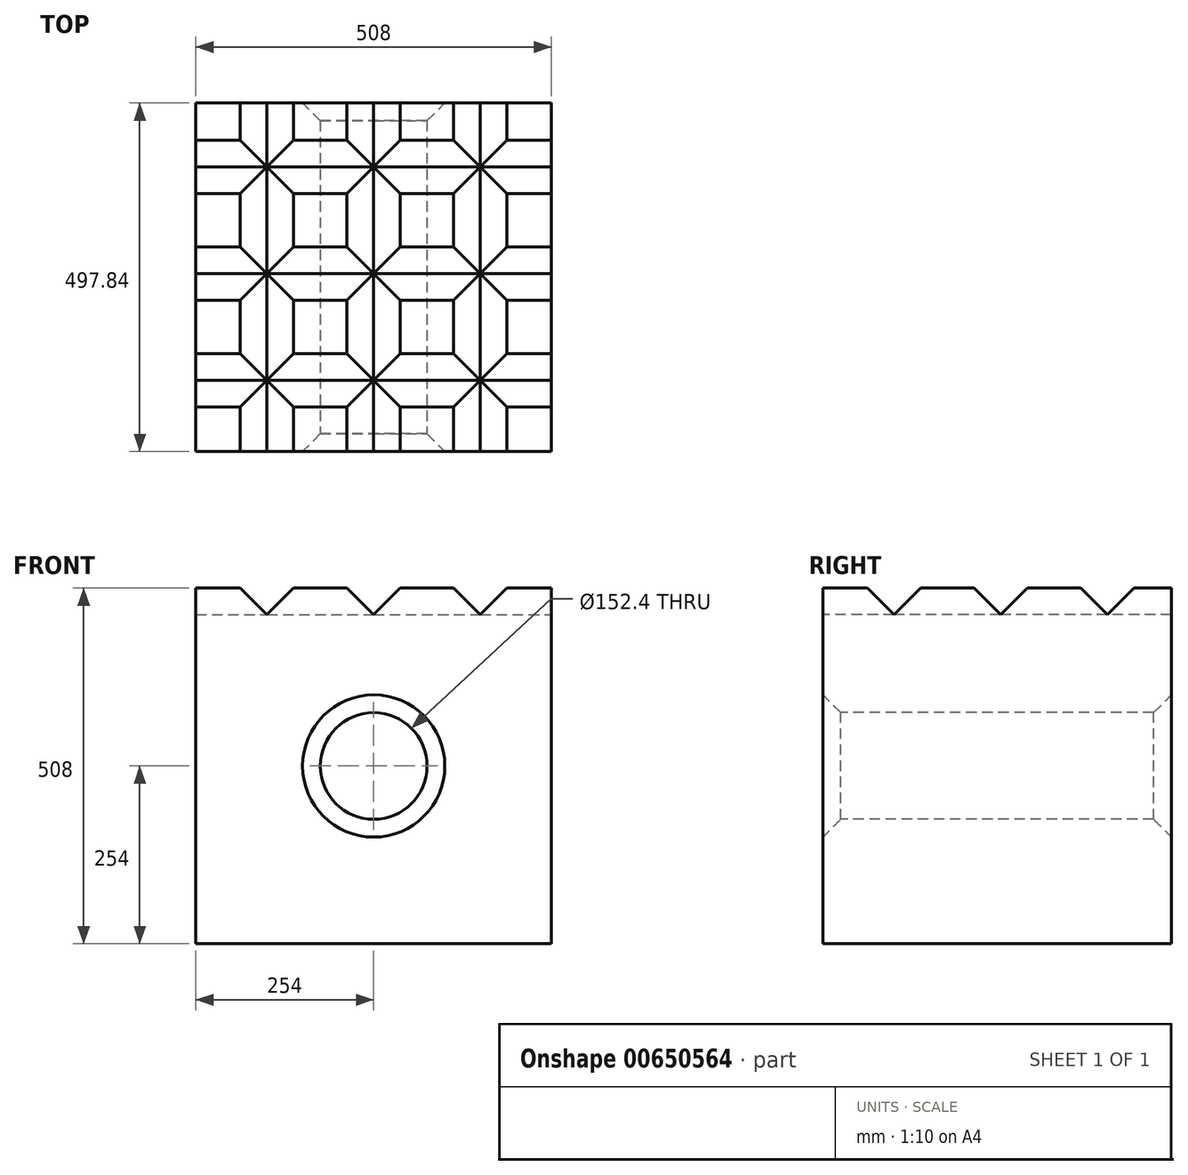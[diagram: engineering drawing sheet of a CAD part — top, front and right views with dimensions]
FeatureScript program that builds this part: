
annotation { "Feature Type Name" : "Feature", "Feature Type Description" : "" }
export const myFeature = defineFeature(function(context is Context, id is Id, definition is map)
    precondition{}
    {
        {
            var Q0;
            Q0=qCreatedBy(makeId("Front.planeOp"),FACE);
            var sketch = newSketch(context, id + "F0", { "sketchPlane" : qUnion([Q0])});
            skLineSegment(sketch, "E0.bottom", {"start": v(-254, -254) * mm, "end": v(254, -254) * mm});
            skLineSegment(sketch, "E0.top", {"start": v(-254, 254) * mm, "end": v(254, 254) * mm});
            skLineSegment(sketch, "E0.left", {"start": v(-254, -254) * mm, "end": v(-254, 254) * mm});
            skLineSegment(sketch, "E0.right", {"start": v(254, -254) * mm, "end": v(254, 254) * mm});
            skPoint(sketch, "E0.middle", {"position": v(0, 0) * mm});
            skSolve(sketch);
        }
        {
            var Q0;
            Q0=makeQuery(id+"F0.imprint","IMPRINT",FACE,{"disambiguationData":[TD([[makeQuery(id+"F0.imprint","IMPRINT",EDGE,{"derivedFrom":sQuery(id+"F0.wireOp",EDGE,"E0.bottom")}),1.0]])]});
            extrude(context, id + "F1", {"entities" : qUnion([Q0]), "depth" : 497.84 * mm, "offsetDistance" : 25.4 * mm});
        }
        {
            var Q0;
            Q0=makeQuery(id+"F1.opExtrude","CAP_FACE",FACE,{"disambiguationData":[OSD([sQuery(id+"F0.wireOp",EDGE,"E0.bottom"),sQuery(id+"F0.wireOp",EDGE,"E0.top"),sQuery(id+"F0.wireOp",EDGE,"E0.left"),sQuery(id+"F0.wireOp",EDGE,"E0.right")])],"isStart":false});
            var sketch = newSketch(context, id + "F2", { "sketchPlane" : qUnion([Q0])});
            skCircle(sketch, "E1", {"center": v(0, 0) * mm, "radius": 76.2 * mm});
            skSolve(sketch);
        }
        {
            var Q0;
            Q0=makeQuery(id+"F2.imprint","IMPRINT",FACE,{"disambiguationData":[TD([[makeQuery(id+"F2.imprint","IMPRINT",EDGE,{"derivedFrom":sQuery(id+"F2.wireOp",EDGE,"E1")}),1.0]])]});
            extrude(context, id + "F3", {"entities" : qUnion([Q0]), "operationType" : NewBodyOperationType.REMOVE, "endBound" : BoundingType.SYMMETRIC, "oppositeDirection" : true, "depth" : 1356.5 * mm, "offsetDistance" : 25.4 * mm});
        }
        {
            var Q0;
            Q0=makeQuery(id+"F3.boolean.opBoolean","INTERSECT",EDGE,{"derivedFrom":[makeQuery(id+"F1.opExtrude","CAP_FACE",FACE,{"disambiguationData":[OSD([sQuery(id+"F0.wireOp",EDGE,"E0.bottom"),sQuery(id+"F0.wireOp",EDGE,"E0.top"),sQuery(id+"F0.wireOp",EDGE,"E0.left"),sQuery(id+"F0.wireOp",EDGE,"E0.right")])],"isStart":false}),makeQuery(id+"F3.opExtrude","SWEPT_FACE",FACE,{"disambiguationData":[OSD([sQuery(id+"F2.wireOp",EDGE,"E1")])]})]});
            var Q1;
            Q1=makeQuery(id+"F3.boolean.opBoolean","INTERSECT",EDGE,{"derivedFrom":[makeQuery(id+"F1.opExtrude","CAP_FACE",FACE,{"disambiguationData":[OSD([sQuery(id+"F0.wireOp",EDGE,"E0.bottom"),sQuery(id+"F0.wireOp",EDGE,"E0.top"),sQuery(id+"F0.wireOp",EDGE,"E0.left"),sQuery(id+"F0.wireOp",EDGE,"E0.right")])],"isStart":true}),makeQuery(id+"F3.opExtrude","SWEPT_FACE",FACE,{"disambiguationData":[OSD([sQuery(id+"F2.wireOp",EDGE,"E1")])]})]});
            chamfer(context, id + "F4", {"entities" : qUnion([Q0, Q1]), "width" : 25.4 * mm, "tangentPropagation" : true});
        }
        {
            var Q0;
            Q0=qCreatedBy(makeId("Front.planeOp"),FACE);
            var sketch = newSketch(context, id + "F5", { "sketchPlane" : qUnion([Q0])});
            skLineSegment(sketch, "E2", {"start": v(-152.4, 215.9) * mm, "end": v(-98.52, 269.78) * mm});
            skLineSegment(sketch, "E3", {"start": v(-98.52, 269.78) * mm, "end": v(-206.28, 269.78) * mm});
            skLineSegment(sketch, "E4", {"start": v(-206.28, 269.78) * mm, "end": v(-152.4, 215.9) * mm});
            skSolve(sketch);
        }
        {
            var Q0;
            Q0=makeQuery(id+"F5.imprint","IMPRINT",FACE,{"disambiguationData":[TD([[makeQuery(id+"F5.imprint","IMPRINT",EDGE,{"derivedFrom":sQuery(id+"F5.wireOp",EDGE,"E2")}),1.0]])]});
            extrude(context, id + "F6", {"entities" : qUnion([Q0]), "operationType" : NewBodyOperationType.REMOVE, "endBound" : BoundingType.SYMMETRIC, "oppositeDirection" : true, "depth" : 1270 * mm, "offsetDistance" : 25.4 * mm});
        }
        {
            var Q0;
            Q0=qCreatedBy(makeId("Front.planeOp"),FACE);
            var sketch = newSketch(context, id + "F7", { "sketchPlane" : qUnion([Q0])});
            skLineSegment(sketch, "E5", {"start": v(0, 215.9) * mm, "end": v(53.88, 269.78) * mm});
            skLineSegment(sketch, "E6", {"start": v(53.88, 269.78) * mm, "end": v(-53.88, 269.78) * mm});
            skLineSegment(sketch, "E7", {"start": v(-53.88, 269.78) * mm, "end": v(0, 215.9) * mm});
            skSolve(sketch);
        }
        {
            var Q0;
            Q0 = qSketchRegion(id + "F7", true);
            extrude(context, id + "F8", {"entities" : qUnion([Q0]), "operationType" : NewBodyOperationType.REMOVE, "endBound" : BoundingType.SYMMETRIC, "oppositeDirection" : true, "depth" : 1270 * mm, "offsetDistance" : 25.4 * mm});
        }
        {
            var Q0;
            Q0=qCreatedBy(makeId("Front.planeOp"),FACE);
            var sketch = newSketch(context, id + "F9", { "sketchPlane" : qUnion([Q0])});
            skLineSegment(sketch, "E8", {"start": v(152.4, 215.9) * mm, "end": v(206.28, 269.78) * mm});
            skLineSegment(sketch, "E9", {"start": v(206.28, 269.78) * mm, "end": v(98.52, 269.78) * mm});
            skLineSegment(sketch, "E10", {"start": v(152.4, 215.9) * mm, "end": v(98.52, 269.78) * mm});
            skSolve(sketch);
        }
        {
            var Q0;
            Q0 = qSketchRegion(id + "F9", true);
            extrude(context, id + "F10", {"entities" : qUnion([Q0]), "operationType" : NewBodyOperationType.REMOVE, "endBound" : BoundingType.SYMMETRIC, "oppositeDirection" : true, "depth" : 1270 * mm, "offsetDistance" : 25.4 * mm});
        }
        {
            var Q0;
            Q0=qCreatedBy(makeId("Right.planeOp"),FACE);
            var sketch = newSketch(context, id + "F11", { "sketchPlane" : qUnion([Q0])});
            skLineSegment(sketch, "E11", {"start": v(-91.44, 215.9) * mm, "end": v(-37.56, 269.78) * mm});
            skLineSegment(sketch, "E12", {"start": v(-37.56, 269.78) * mm, "end": v(-145.32, 269.78) * mm});
            skLineSegment(sketch, "E13", {"start": v(-145.32, 269.78) * mm, "end": v(-91.44, 215.9) * mm});
            skSolve(sketch);
        }
        {
            var Q0;
            Q0 = qSketchRegion(id + "F11", true);
            extrude(context, id + "F12", {"entities" : qUnion([Q0]), "operationType" : NewBodyOperationType.REMOVE, "endBound" : BoundingType.SYMMETRIC, "oppositeDirection" : true, "depth" : 1270 * mm, "offsetDistance" : 25.4 * mm});
        }
        {
            var Q0;
            Q0=qCreatedBy(makeId("Right.planeOp"),FACE);
            var sketch = newSketch(context, id + "F13", { "sketchPlane" : qUnion([Q0])});
            skLineSegment(sketch, "E14", {"start": v(-243.84, 215.9) * mm, "end": v(-189.96, 269.78) * mm});
            skLineSegment(sketch, "E15", {"start": v(-189.96, 269.78) * mm, "end": v(-297.72, 269.78) * mm});
            skLineSegment(sketch, "E16", {"start": v(-297.72, 269.78) * mm, "end": v(-243.84, 215.9) * mm});
            skSolve(sketch);
        }
        {
            var Q0;
            Q0 = qSketchRegion(id + "F13", true);
            extrude(context, id + "F14", {"entities" : qUnion([Q0]), "operationType" : NewBodyOperationType.REMOVE, "endBound" : BoundingType.SYMMETRIC, "oppositeDirection" : true, "depth" : 1270 * mm, "offsetDistance" : 25.4 * mm});
        }
        {
            var Q0;
            Q0=qCreatedBy(makeId("Right.planeOp"),FACE);
            var sketch = newSketch(context, id + "F15", { "sketchPlane" : qUnion([Q0])});
            skLineSegment(sketch, "E17", {"start": v(-396.24, 215.9) * mm, "end": v(-342.36, 269.78) * mm});
            skLineSegment(sketch, "E18", {"start": v(-342.36, 269.78) * mm, "end": v(-450.12, 269.78) * mm});
            skLineSegment(sketch, "E19", {"start": v(-396.24, 215.9) * mm, "end": v(-450.12, 269.78) * mm});
            skSolve(sketch);
        }
        {
            var Q0;
            Q0 = qSketchRegion(id + "F15", true);
            extrude(context, id + "F16", {"entities" : qUnion([Q0]), "operationType" : NewBodyOperationType.REMOVE, "endBound" : BoundingType.SYMMETRIC, "oppositeDirection" : true, "depth" : 1270 * mm, "offsetDistance" : 25.4 * mm});
        }
    });
